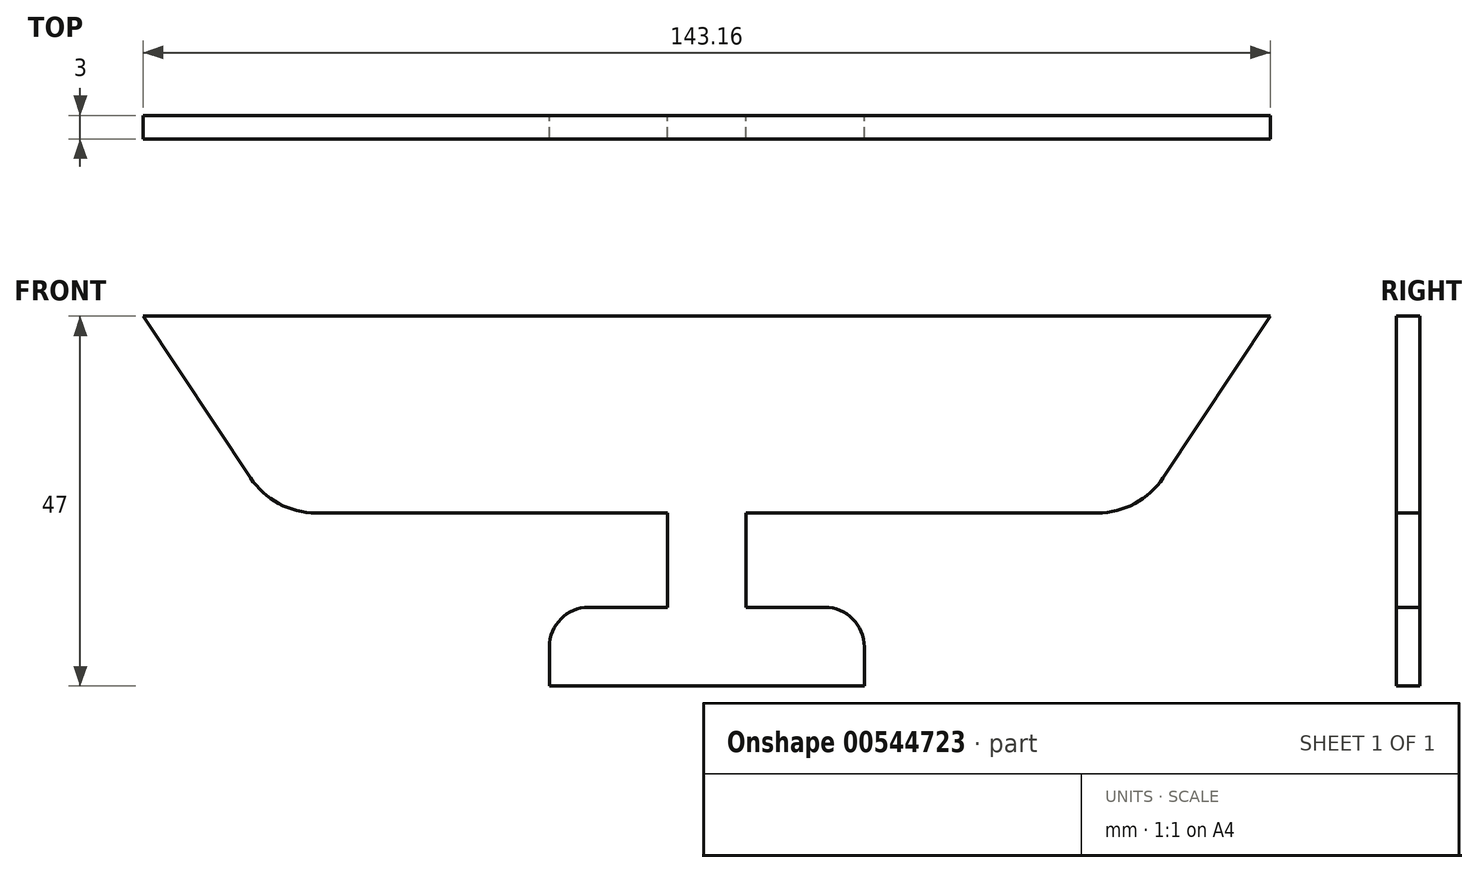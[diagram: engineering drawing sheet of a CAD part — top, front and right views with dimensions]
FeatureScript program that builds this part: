
annotation { "Feature Type Name" : "Feature", "Feature Type Description" : "" }
export const myFeature = defineFeature(function(context is Context, id is Id, definition is map)
    precondition{}
    {
        {
            var Q0;
            Q0=qCreatedBy(makeId("Front.planeOp"),FACE);
            var sketch = newSketch(context, id + "F0", { "sketchPlane" : qUnion([Q0])});
            skLineSegment(sketch, "E0", {"start": v(0, 0) * mm, "end": v(-50, 0) * mm});
            skLineSegment(sketch, "E1", {"start": v(0, 0) * mm, "end": v(0, -12) * mm});
            skLineSegment(sketch, "E2", {"start": v(0, -12) * mm, "end": v(-15, -12) * mm});
            skLineSegment(sketch, "E3", {"start": v(-15, -12) * mm, "end": v(-15, -22) * mm});
            skLineSegment(sketch, "E4", {"start": v(-15, -22) * mm, "end": v(25, -22) * mm});
            skLineSegment(sketch, "E5", {"start": v(25, -22) * mm, "end": v(25, -12) * mm});
            skLineSegment(sketch, "E6", {"start": v(25, -12) * mm, "end": v(10, -12) * mm});
            skLineSegment(sketch, "E7", {"start": v(10, -12) * mm, "end": v(10, 0) * mm});
            skLineSegment(sketch, "E8", {"start": v(10, 0) * mm, "end": v(60, 0) * mm});
            skLineSegment(sketch, "E9", {"start": v(-50, 0) * mm, "end": v(-66.58, 25) * mm});
            skLineSegment(sketch, "E10", {"start": v(60, 0) * mm, "end": v(76.58, 25) * mm});
            skLineSegment(sketch, "E11", {"start": v(-66.58, 25) * mm, "end": v(76.58, 25) * mm});
            skSolve(sketch);
        }
        {
            var Q0;
            Q0=qSketchRegion(id+"F0",true);
            extrude(context, id + "F1", {"entities" : qUnion([Q0]), "depth" : 3 * mm});
        }
        {
            var Q0;
            Q0=makeQuery(id+"F1.opExtrude","SWEPT_EDGE",EDGE,{"disambiguationData":[OSD([sQuery(id+"F0.wireOp",EDGE,"E5"),sQuery(id+"F0.wireOp",EDGE,"E6")])]});
            fillet(context, id + "F2", {"entities" : qUnion([Q0]), "radius" : 5 * mm, "tangentPropagation" : true, "allowEdgeOverflow" : false});
        }
        {
            var Q0;
            Q0=makeQuery(id+"F1.opExtrude","SWEPT_EDGE",EDGE,{"disambiguationData":[OSD([sQuery(id+"F0.wireOp",EDGE,"E2"),sQuery(id+"F0.wireOp",EDGE,"E3")])]});
            fillet(context, id + "F3", {"entities" : qUnion([Q0]), "radius" : 5 * mm, "tangentPropagation" : true, "allowEdgeOverflow" : false});
        }
        {
            var Q0;
            Q0=makeQuery(id+"F1.opExtrude","SWEPT_EDGE",EDGE,{"disambiguationData":[OSD([sQuery(id+"F0.wireOp",EDGE,"E8"),sQuery(id+"F0.wireOp",EDGE,"E10")])]});
            fillet(context, id + "F4", {"entities" : qUnion([Q0]), "radius" : 10 * mm, "tangentPropagation" : true, "allowEdgeOverflow" : false});
        }
        {
            var Q0;
            Q0=makeQuery(id+"F1.opExtrude","SWEPT_EDGE",EDGE,{"disambiguationData":[OSD([sQuery(id+"F0.wireOp",EDGE,"E0"),sQuery(id+"F0.wireOp",EDGE,"E9")])]});
            fillet(context, id + "F5", {"entities" : qUnion([Q0]), "radius" : 10 * mm, "tangentPropagation" : true, "allowEdgeOverflow" : false});
        }
    });
